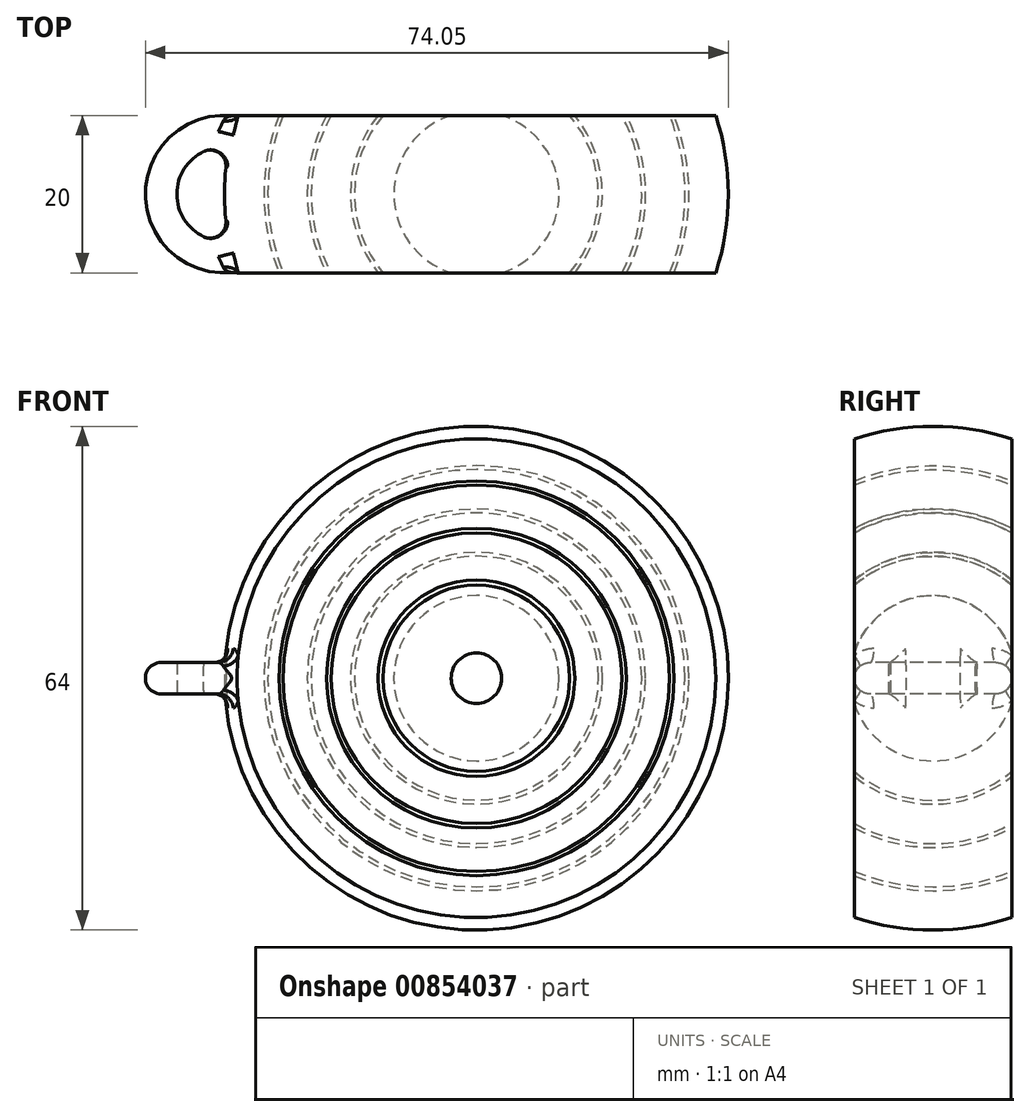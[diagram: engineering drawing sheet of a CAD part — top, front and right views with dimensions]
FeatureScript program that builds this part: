
annotation { "Feature Type Name" : "Feature", "Feature Type Description" : "" }
export const myFeature = defineFeature(function(context is Context, id is Id, definition is map)
    precondition{}
    {
        {
            var Q0;
            Q0=qCreatedBy(makeId("Top.planeOp"),FACE);
            var sketch = newSketch(context, id + "F0", { "sketchPlane" : qUnion([Q0])});
            skArc(sketch, "E0", {"start": v(0, -10) * mm, "mid": v(10, 0) * mm, "end": v(0, 10) * mm});
            skArc(sketch, "E1", {"start": v(-3.2, 10) * mm, "mid": v(-10.5, 0) * mm, "end": v(-3.2, -10) * mm});
            skArc(sketch, "E2", {"start": v(-11.84, 10) * mm, "mid": v(-15.5, 0) * mm, "end": v(-11.84, -10) * mm});
            skArc(sketch, "E3", {"start": v(-12.49, 10) * mm, "mid": v(-16, 0) * mm, "end": v(-12.49, -10) * mm});
            skArc(sketch, "E4", {"start": v(-18.47, 10) * mm, "mid": v(-21, 0) * mm, "end": v(-18.47, -10) * mm});
            skArc(sketch, "E5", {"start": v(-19.03, 10) * mm, "mid": v(-21.5, 0) * mm, "end": v(-19.03, -10) * mm});
            skArc(sketch, "E6", {"start": v(-24.54, 10) * mm, "mid": v(-26.5, 0) * mm, "end": v(-24.54, -10) * mm});
            skArc(sketch, "E7", {"start": v(-25.08, 10) * mm, "mid": v(-27, 0) * mm, "end": v(-25.08, -10) * mm});
            skArc(sketch, "E8", {"start": v(-30.4, 10) * mm, "mid": v(-32, 0) * mm, "end": v(-30.4, -10) * mm});
            skLineSegment(sketch, "E9", {"start": v(-30.4, 10) * mm, "end": v(30.4, 10) * mm});
            skLineSegment(sketch, "E10", {"start": v(-30.4, -10) * mm, "end": v(30.4, -10) * mm});
            skArc(sketch, "E11.trimOffspring", {"start": v(3.2, -10) * mm, "mid": v(10.5, 0) * mm, "end": v(3.2, 10) * mm});
            skArc(sketch, "E12.trimOffspring", {"start": v(11.84, -10) * mm, "mid": v(15.5, 0) * mm, "end": v(11.84, 10) * mm});
            skArc(sketch, "E13.trimOffspring", {"start": v(12.49, -10) * mm, "mid": v(16, 0) * mm, "end": v(12.49, 10) * mm});
            skArc(sketch, "E14.trimOffspring", {"start": v(18.47, -10) * mm, "mid": v(21, 0) * mm, "end": v(18.47, 10) * mm});
            skArc(sketch, "E15.trimOffspring", {"start": v(19.03, -10) * mm, "mid": v(21.5, 0) * mm, "end": v(19.03, 10) * mm});
            skArc(sketch, "E16.trimOffspring", {"start": v(24.54, -10) * mm, "mid": v(26.5, 0) * mm, "end": v(24.54, 10) * mm});
            skArc(sketch, "E17.trimOffspring", {"start": v(25.08, -10) * mm, "mid": v(27, 0) * mm, "end": v(25.08, 10) * mm});
            skArc(sketch, "E18.trimOffspring", {"start": v(30.4, -10) * mm, "mid": v(32, 0) * mm, "end": v(30.4, 10) * mm});
            skLineSegment(sketch, "E19", {"start": v(0, 18.4) * mm, "end": v(0, -17.7) * mm});
            skSolve(sketch);
        }
        {
            var Q0;
            {var subQ0=sQuery(id+"F0.wireOp",EDGE,"E7");Q0=makeQuery(id+"F0.imprint","IMPRINT",FACE,{"disambiguationData":[TD([[makeQuery(id+"F0.imprint","IMPRINT",EDGE,{"derivedFrom":subQ0}),-1.0]])]});}
            var Q1;
            {var subQ0=sQuery(id+"F0.wireOp",EDGE,"E5");Q1=makeQuery(id+"F0.imprint","IMPRINT",FACE,{"disambiguationData":[TD([[makeQuery(id+"F0.imprint","IMPRINT",EDGE,{"derivedFrom":subQ0}),-1.0]])]});}
            var Q2;
            {var subQ0=sQuery(id+"F0.wireOp",EDGE,"E3");Q2=makeQuery(id+"F0.imprint","IMPRINT",FACE,{"disambiguationData":[TD([[makeQuery(id+"F0.imprint","IMPRINT",EDGE,{"derivedFrom":subQ0}),-1.0]])]});}
            var Q3;
            {var subQ0=sQuery(id+"F0.wireOp",EDGE,"E1");Q3=makeQuery(id+"F0.imprint","IMPRINT",FACE,{"disambiguationData":[TD([[makeQuery(id+"F0.imprint","IMPRINT",EDGE,{"derivedFrom":subQ0}),-1.0]])]});}
            var Q4;
            Q4=sQuery(id+"F0.wireOp",EDGE,"E19");
            revolve(context, id + "F1", {"surfaceOperationType" : NewSurfaceOperationType.NEW, "entities" : qUnion([Q0, Q1, Q2, Q3]), "axis" : qUnion([Q4]), "revolveType" : RevolveType.FULL});
        }
        {
            var Q0;
            Q0=qCreatedBy(makeId("Top.planeOp"),FACE);
            var sketch = newSketch(context, id + "F2", { "sketchPlane" : qUnion([Q0])});
            skArc(sketch, "E20", {"start": v(-28.08, 9.18) * mm, "mid": v(-42.05, 0) * mm, "end": v(-28.08, -9.18) * mm});
            skArc(sketch, "E21", {"start": v(-28.08, 4.5) * mm, "mid": v(-38.05, 0) * mm, "end": v(-28.08, -4.5) * mm});
            skLineSegment(sketch, "E22", {"start": v(-28.08, -9.18) * mm, "end": v(-28.08, -4.5) * mm});
            skLineSegment(sketch, "E23", {"start": v(-28.08, 4.5) * mm, "end": v(-28.08, 9.18) * mm});
            skSolve(sketch);
        }
        {
            var Q0;
            Q0=makeQuery(id+"F2.imprint","IMPRINT",FACE,{"disambiguationData":[TD([[makeQuery(id+"F2.imprint","IMPRINT",EDGE,{"derivedFrom":sQuery(id+"F2.wireOp",EDGE,"E20")}),1.0]])]});
            extrude(context, id + "F3", {"entities" : qUnion([Q0]), "operationType" : NewBodyOperationType.ADD, "endBound" : BoundingType.SYMMETRIC, "depth" : 4 * mm, "offsetDistance" : 25 * mm});
        }
        {
            var Q0;
            Q0=makeQuery(id+"F3.opExtrude","CAP_EDGE",EDGE,{"disambiguationData":[OSD([sQuery(id+"F2.wireOp",EDGE,"E20")])],"isStart":true});
            var Q1;
            Q1=makeQuery(id+"F3.opExtrude","CAP_EDGE",EDGE,{"disambiguationData":[OSD([sQuery(id+"F2.wireOp",EDGE,"E20")])],"isStart":false});
            fillet(context, id + "F4", {"entities" : qUnion([Q0, Q1]), "radius" : 2 * mm, "tangentPropagation" : true, "allowEdgeOverflow" : false});
        }
        {
            var Q0;
            Q0=makeQuery(id+"F3.boolean.opBoolean","INTERSECT",EDGE,{"disambiguationData":[OD(1.0)],"derivedFrom":[makeQuery(id+"F1.opRevolve","SWEPT_FACE",FACE,{"disambiguationData":[OSD([sQuery(id+"F0.wireOp",EDGE,"E8")])]}),makeQuery(id+"F3.opExtrude","SWEPT_FACE",FACE,{"disambiguationData":[OSD([sQuery(id+"F2.wireOp",EDGE,"E21")])]})]});
            var Q1;
            Q1=makeQuery(id+"F3.boolean.opBoolean","INTERSECT",EDGE,{"disambiguationData":[OD(0.0)],"derivedFrom":[makeQuery(id+"F1.opRevolve","SWEPT_FACE",FACE,{"disambiguationData":[OSD([sQuery(id+"F0.wireOp",EDGE,"E8")])]}),makeQuery(id+"F3.opExtrude","SWEPT_FACE",FACE,{"disambiguationData":[OSD([sQuery(id+"F2.wireOp",EDGE,"E21")])]})]});
            var Q2;
            Q2=makeQuery(id+"F3.boolean.opBoolean","INTERSECT",EDGE,{"disambiguationData":[OD(0.0)],"derivedFrom":[makeQuery(id+"F1.opRevolve","SWEPT_FACE",FACE,{"disambiguationData":[OSD([sQuery(id+"F0.wireOp",EDGE,"E8")])]}),makeQuery(id+"F3.opExtrude","CAP_FACE",FACE,{"disambiguationData":[OSD([sQuery(id+"F2.wireOp",EDGE,"E20"),sQuery(id+"F2.wireOp",EDGE,"E21"),sQuery(id+"F2.wireOp",EDGE,"E22"),sQuery(id+"F2.wireOp",EDGE,"E23")])],"isStart":true})]});
            var Q3;
            Q3=makeQuery(id+"F3.boolean.opBoolean","INTERSECT",EDGE,{"disambiguationData":[OD(1.0)],"derivedFrom":[makeQuery(id+"F1.opRevolve","SWEPT_FACE",FACE,{"disambiguationData":[OSD([sQuery(id+"F0.wireOp",EDGE,"E8")])]}),makeQuery(id+"F3.opExtrude","CAP_FACE",FACE,{"disambiguationData":[OSD([sQuery(id+"F2.wireOp",EDGE,"E20"),sQuery(id+"F2.wireOp",EDGE,"E21"),sQuery(id+"F2.wireOp",EDGE,"E22"),sQuery(id+"F2.wireOp",EDGE,"E23")])],"isStart":true})]});
            fillet(context, id + "F5", {"entities" : qUnion([Q0, Q1, Q2, Q3]), "radius" : 2 * mm, "tangentPropagation" : true, "allowEdgeOverflow" : false});
        }
    });
